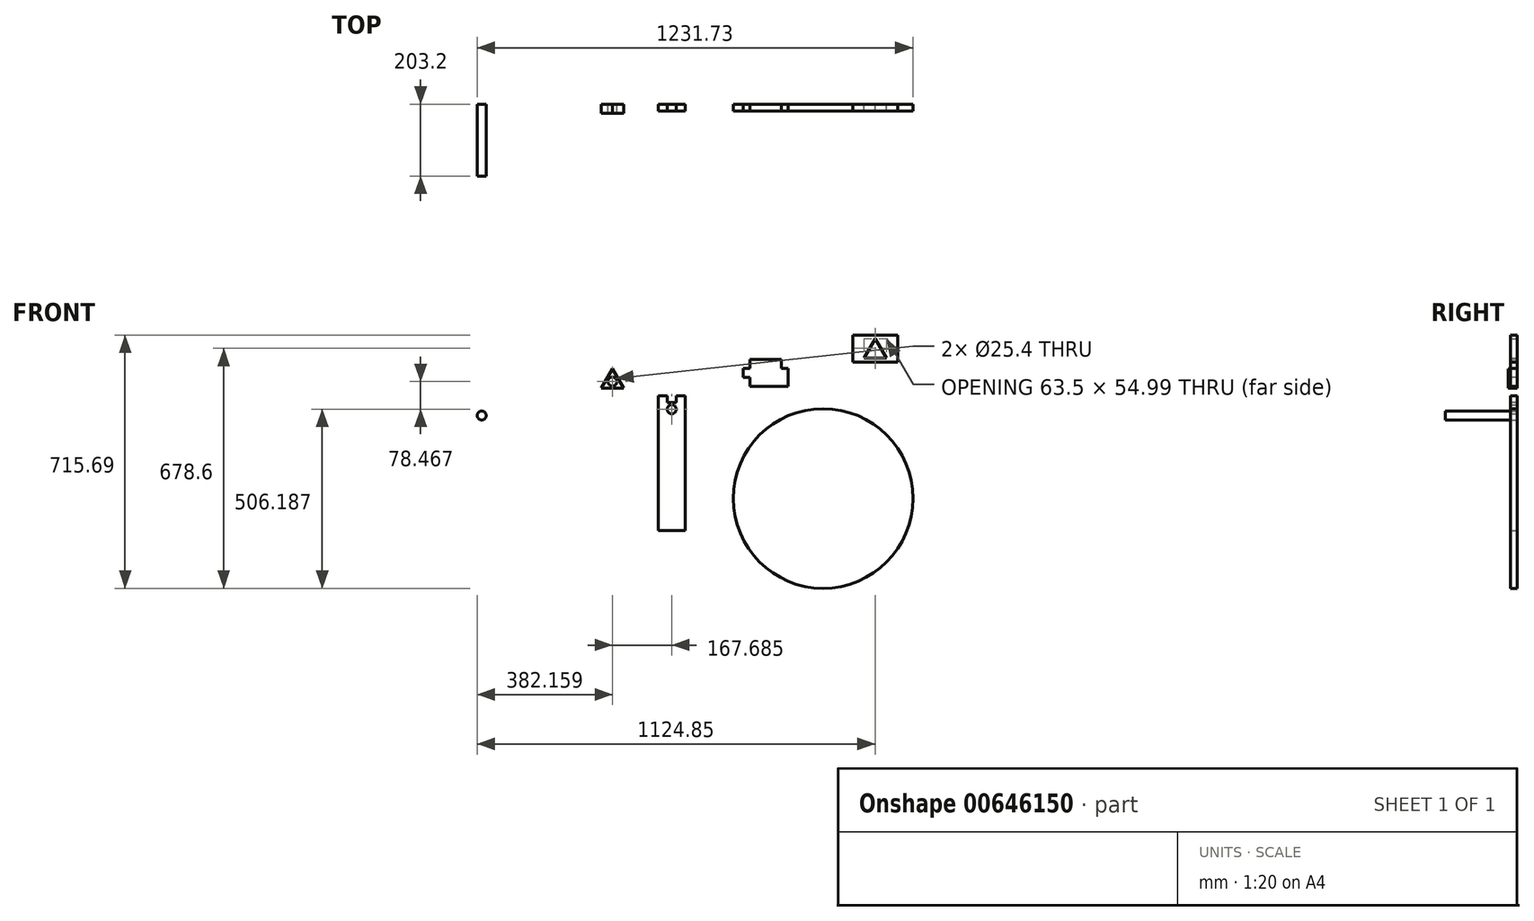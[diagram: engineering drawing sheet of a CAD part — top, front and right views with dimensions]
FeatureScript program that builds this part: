
annotation { "Feature Type Name" : "Feature", "Feature Type Description" : "" }
export const myFeature = defineFeature(function(context is Context, id is Id, definition is map)
    precondition{}
    {
        {
            var Q0;
            Q0=qCreatedBy(makeId("Front.planeOp"),FACE);
            var sketch = newSketch(context, id + "F0", { "sketchPlane" : qUnion([Q0])});
            skLineSegment(sketch, "E0.bottom", {"start": v(-82.53, 327.54) * mm, "end": v(-6.33, 327.54) * mm});
            skLineSegment(sketch, "E0.top", {"start": v(-82.53, -53.46) * mm, "end": v(-6.33, -53.46) * mm});
            skLineSegment(sketch, "E0.left", {"start": v(-82.53, 327.54) * mm, "end": v(-82.53, -53.46) * mm});
            skLineSegment(sketch, "E0.right", {"start": v(-6.33, 327.54) * mm, "end": v(-6.33, -53.46) * mm});
            skCircle(sketch, "E1", {"center": v(-44.43, 289.44) * mm, "radius": 12.7 * mm});
            skLineSegment(sketch, "E2.bottom", {"start": v(-82.53, 327.54) * mm, "end": v(-69.83, 327.54) * mm});
            skLineSegment(sketch, "E2.top", {"start": v(-82.53, 308.49) * mm, "end": v(-69.83, 308.49) * mm});
            skLineSegment(sketch, "E2.left", {"start": v(-82.53, 327.54) * mm, "end": v(-82.53, 308.49) * mm});
            skLineSegment(sketch, "E3.bottom", {"start": v(-69.83, 327.54) * mm, "end": v(-57.13, 327.54) * mm});
            skLineSegment(sketch, "E3.top", {"start": v(-69.83, 308.49) * mm, "end": v(-57.13, 308.49) * mm});
            skLineSegment(sketch, "E3.right", {"start": v(-57.13, 327.54) * mm, "end": v(-57.13, 308.49) * mm});
            skLineSegment(sketch, "E4.bottom", {"start": v(-57.13, 327.54) * mm, "end": v(-44.43, 327.54) * mm});
            skLineSegment(sketch, "E4.top", {"start": v(-57.13, 308.49) * mm, "end": v(-44.43, 308.49) * mm});
            skLineSegment(sketch, "E5.bottom", {"start": v(-44.43, 327.54) * mm, "end": v(-31.73, 327.54) * mm});
            skLineSegment(sketch, "E5.top", {"start": v(-44.43, 308.49) * mm, "end": v(-31.73, 308.49) * mm});
            skLineSegment(sketch, "E6.bottom", {"start": v(-31.73, 327.54) * mm, "end": v(-19.03, 327.54) * mm});
            skLineSegment(sketch, "E6.top", {"start": v(-31.73, 308.49) * mm, "end": v(-19.03, 308.49) * mm});
            skLineSegment(sketch, "E6.left", {"start": v(-31.73, 327.54) * mm, "end": v(-31.73, 308.49) * mm});
            skLineSegment(sketch, "E7.bottom", {"start": v(-19.03, 327.54) * mm, "end": v(-6.33, 327.54) * mm});
            skLineSegment(sketch, "E7.top", {"start": v(-19.03, 308.49) * mm, "end": v(-6.33, 308.49) * mm});
            skLineSegment(sketch, "E7.right", {"start": v(-6.33, 327.54) * mm, "end": v(-6.33, 308.49) * mm});
            skSolve(sketch);
        }
        {
            var Q0;
            Q0 = qSketchRegion(id + "F0", true);
            var Q1;
            Q1=makeQuery(id+"F0.imprint","IMPRINT",FACE,{"disambiguationData":[TD([[makeQuery(id+"F0.imprint","IMPRINT",EDGE,{"derivedFrom":sQuery(id+"F0.wireOp",EDGE,"E0.bottom")}),-1.0]])]});
            extrude(context, id + "F1", {"entities" : qUnion([Q0, Q1]), "depth" : 19.05 * mm, "offsetDistance" : 25.4 * mm});
        }
        {
            var Q0;
            Q0=qCreatedBy(makeId("Front.planeOp"),FACE);
            var sketch = newSketch(context, id + "F2", { "sketchPlane" : qUnion([Q0])});
            skLineSegment(sketch, "E8.bottom", {"start": v(157.89, 430.1) * mm, "end": v(284.89, 430.1) * mm});
            skLineSegment(sketch, "E8.top", {"start": v(157.89, 353.9) * mm, "end": v(284.89, 353.9) * mm});
            skLineSegment(sketch, "E8.left", {"start": v(157.89, 430.1) * mm, "end": v(157.89, 353.9) * mm});
            skLineSegment(sketch, "E8.right", {"start": v(284.89, 430.1) * mm, "end": v(284.89, 353.9) * mm});
            skSolve(sketch);
        }
        {
            var Q0;
            Q0 = qSketchRegion(id + "F2", true);
            extrude(context, id + "F3", {"entities" : qUnion([Q0]), "depth" : 19.05 * mm, "offsetDistance" : 25.4 * mm});
        }
        {
            var Q0;
            Q0=qCreatedBy(makeId("Front.planeOp"),FACE);
            var sketch = newSketch(context, id + "F4", { "sketchPlane" : qUnion([Q0])});
            skCircle(sketch, "E9", {"center": v(383.46, 37.25) * mm, "radius": 254 * mm});
            skSolve(sketch);
        }
        {
            var Q0;
            Q0 = qSketchRegion(id + "F4", true);
            extrude(context, id + "F5", {"entities" : qUnion([Q0]), "operationType" : NewBodyOperationType.ADD, "depth" : 19.05 * mm, "offsetDistance" : 25.4 * mm});
        }
        {
            var Q0;
            Q0=qCreatedBy(makeId("Front.planeOp"),FACE);
            var sketch = newSketch(context, id + "F6", { "sketchPlane" : qUnion([Q0])});
            skLineSegment(sketch, "E10.bottom", {"start": v(467.08, 498.94) * mm, "end": v(594.08, 498.94) * mm});
            skLineSegment(sketch, "E10.top", {"start": v(467.08, 422.74) * mm, "end": v(594.08, 422.74) * mm});
            skLineSegment(sketch, "E10.left", {"start": v(467.08, 498.94) * mm, "end": v(467.08, 422.74) * mm});
            skLineSegment(sketch, "E10.right", {"start": v(594.08, 498.94) * mm, "end": v(594.08, 422.74) * mm});
            skLineSegment(sketch, "E11", {"start": v(498.83, 434.35) * mm, "end": v(562.33, 434.35) * mm});
            skLineSegment(sketch, "E12", {"start": v(562.33, 434.35) * mm, "end": v(530.58, 489.35) * mm});
            skLineSegment(sketch, "E13", {"start": v(530.58, 489.35) * mm, "end": v(498.83, 434.35) * mm});
            skSolve(sketch);
        }
        {
            var Q0;
            Q0=makeQuery(id+"F6.imprint","IMPRINT",FACE,{"disambiguationData":[TD([[makeQuery(id+"F6.imprint","IMPRINT",EDGE,{"derivedFrom":sQuery(id+"F6.wireOp",EDGE,"E10.bottom")}),-1.0]])]});
            extrude(context, id + "F7", {"entities" : qUnion([Q0]), "depth" : 19.05 * mm, "offsetDistance" : 25.4 * mm});
        }
        {
            var Q0;
            Q0=makeQuery(id+"F1.opExtrude","CAP_FACE",FACE,{"disambiguationData":[OSD([sQuery(id+"F0.wireOp",EDGE,"E0.top"),sQuery(id+"F0.wireOp",EDGE,"E0.left"),sQuery(id+"F0.wireOp",EDGE,"E0.right"),sQuery(id+"F0.wireOp",EDGE,"E1"),sQuery(id+"F0.wireOp",EDGE,"E2.bottom"),sQuery(id+"F0.wireOp",EDGE,"E2.left"),sQuery(id+"F0.wireOp",EDGE,"E3.bottom"),sQuery(id+"F0.wireOp",EDGE,"E4.bottom"),sQuery(id+"F0.wireOp",EDGE,"E5.bottom"),sQuery(id+"F0.wireOp",EDGE,"E6.bottom"),sQuery(id+"F0.wireOp",EDGE,"E7.bottom"),sQuery(id+"F0.wireOp",EDGE,"E7.right")])],"isStart":false});
            var sketch = newSketch(context, id + "F8", { "sketchPlane" : qUnion([Q0])});
            skLineSegment(sketch, "E14.bottom", {"start": v(-82.53, 327.54) * mm, "end": v(-57.13, 327.54) * mm});
            skLineSegment(sketch, "E14.top", {"start": v(-82.53, 308.49) * mm, "end": v(-57.13, 308.49) * mm});
            skLineSegment(sketch, "E14.left", {"start": v(-82.53, 327.54) * mm, "end": v(-82.53, 308.49) * mm});
            skLineSegment(sketch, "E14.right", {"start": v(-57.13, 327.54) * mm, "end": v(-57.13, 308.49) * mm});
            skLineSegment(sketch, "E15.bottom", {"start": v(-57.13, 327.54) * mm, "end": v(-31.73, 327.54) * mm});
            skLineSegment(sketch, "E15.top", {"start": v(-57.13, 308.49) * mm, "end": v(-31.73, 308.49) * mm});
            skLineSegment(sketch, "E15.right", {"start": v(-31.73, 327.54) * mm, "end": v(-31.73, 308.49) * mm});
            skLineSegment(sketch, "E16.bottom", {"start": v(-31.73, 327.54) * mm, "end": v(-6.33, 327.54) * mm});
            skLineSegment(sketch, "E16.top", {"start": v(-31.73, 308.49) * mm, "end": v(-6.33, 308.49) * mm});
            skLineSegment(sketch, "E16.right", {"start": v(-6.33, 327.54) * mm, "end": v(-6.33, 308.49) * mm});
            skSolve(sketch);
        }
        {
            var Q0;
            Q0=makeQuery(id+"F8.imprint","IMPRINT",FACE,{"disambiguationData":[TD([[makeQuery(id+"F8.imprint","IMPRINT",EDGE,{"derivedFrom":sQuery(id+"F8.wireOp",EDGE,"E15.bottom")}),-1.0]])]});
            extrude(context, id + "F9", {"entities" : qUnion([Q0]), "operationType" : NewBodyOperationType.REMOVE, "oppositeDirection" : true, "depth" : 25.4 * mm, "offsetDistance" : 25.4 * mm});
        }
        {
            var Q0;
            Q0=makeQuery(id+"F3.opExtrude","CAP_FACE",FACE,{"disambiguationData":[OSD([sQuery(id+"F2.wireOp",EDGE,"E8.bottom"),sQuery(id+"F2.wireOp",EDGE,"E8.top"),sQuery(id+"F2.wireOp",EDGE,"E8.left"),sQuery(id+"F2.wireOp",EDGE,"E8.right")])],"isStart":false});
            var sketch = newSketch(context, id + "F10", { "sketchPlane" : qUnion([Q0])});
            skLineSegment(sketch, "E17.bottom", {"start": v(157.89, 430.1) * mm, "end": v(176.94, 430.1) * mm});
            skLineSegment(sketch, "E17.top", {"start": v(157.89, 404.7) * mm, "end": v(176.94, 404.7) * mm});
            skLineSegment(sketch, "E17.left", {"start": v(157.89, 430.1) * mm, "end": v(157.89, 404.7) * mm});
            skLineSegment(sketch, "E17.right", {"start": v(176.94, 430.1) * mm, "end": v(176.94, 404.7) * mm});
            skLineSegment(sketch, "E18.top", {"start": v(157.89, 379.3) * mm, "end": v(176.94, 379.3) * mm});
            skLineSegment(sketch, "E18.left", {"start": v(157.89, 404.7) * mm, "end": v(157.89, 379.3) * mm});
            skLineSegment(sketch, "E18.right", {"start": v(176.94, 404.7) * mm, "end": v(176.94, 379.3) * mm});
            skLineSegment(sketch, "E19.top", {"start": v(157.89, 353.9) * mm, "end": v(176.94, 353.9) * mm});
            skLineSegment(sketch, "E19.left", {"start": v(157.89, 379.3) * mm, "end": v(157.89, 353.9) * mm});
            skLineSegment(sketch, "E19.right", {"start": v(176.94, 379.3) * mm, "end": v(176.94, 353.9) * mm});
            skLineSegment(sketch, "E20.bottom", {"start": v(284.89, 430.1) * mm, "end": v(265.84, 430.1) * mm});
            skLineSegment(sketch, "E20.top", {"start": v(284.89, 404.7) * mm, "end": v(265.84, 404.7) * mm});
            skLineSegment(sketch, "E20.left", {"start": v(284.89, 430.1) * mm, "end": v(284.89, 404.7) * mm});
            skLineSegment(sketch, "E20.right", {"start": v(265.84, 430.1) * mm, "end": v(265.84, 404.7) * mm});
            skLineSegment(sketch, "E21.bottom", {"start": v(265.84, 404.7) * mm, "end": v(284.89, 404.7) * mm});
            skLineSegment(sketch, "E21.top", {"start": v(265.84, 379.3) * mm, "end": v(284.89, 379.3) * mm});
            skLineSegment(sketch, "E21.left", {"start": v(265.84, 404.7) * mm, "end": v(265.84, 379.3) * mm});
            skLineSegment(sketch, "E21.right", {"start": v(284.89, 404.7) * mm, "end": v(284.89, 379.3) * mm});
            skLineSegment(sketch, "E22.top", {"start": v(265.84, 353.9) * mm, "end": v(284.89, 353.9) * mm});
            skLineSegment(sketch, "E22.left", {"start": v(265.84, 379.3) * mm, "end": v(265.84, 353.9) * mm});
            skLineSegment(sketch, "E22.right", {"start": v(284.89, 379.3) * mm, "end": v(284.89, 353.9) * mm});
            skSolve(sketch);
        }
        {
            var Q0;
            Q0=makeQuery(id+"F10.imprint","IMPRINT",FACE,{"disambiguationData":[TD([[makeQuery(id+"F10.imprint","IMPRINT",EDGE,{"derivedFrom":sQuery(id+"F10.wireOp",EDGE,"E17.bottom")}),-1.0]])]});
            var Q1;
            Q1=makeQuery(id+"F10.imprint","IMPRINT",FACE,{"disambiguationData":[TD([[makeQuery(id+"F10.imprint","IMPRINT",EDGE,{"derivedFrom":sQuery(id+"F10.wireOp",EDGE,"E18.top")}),-1.0]])]});
            var Q2;
            Q2=makeQuery(id+"F10.imprint","IMPRINT",FACE,{"disambiguationData":[TD([[makeQuery(id+"F10.imprint","IMPRINT",EDGE,{"derivedFrom":sQuery(id+"F10.wireOp",EDGE,"E21.top")}),-1.0]])]});
            var Q3;
            Q3=makeQuery(id+"F10.imprint","IMPRINT",FACE,{"disambiguationData":[TD([[makeQuery(id+"F10.imprint","IMPRINT",EDGE,{"derivedFrom":sQuery(id+"F10.wireOp",EDGE,"E20.bottom")}),-1.0]])]});
            extrude(context, id + "F11", {"entities" : qUnion([Q0, Q1, Q2, Q3]), "operationType" : NewBodyOperationType.REMOVE, "oppositeDirection" : true, "depth" : 25.4 * mm, "offsetDistance" : 25.4 * mm});
        }
        {
            var Q0;
            Q0=qCreatedBy(makeId("Front.planeOp"),FACE);
            var sketch = newSketch(context, id + "F12", { "sketchPlane" : qUnion([Q0])});
            skLineSegment(sketch, "E23", {"start": v(-244, 348.85) * mm, "end": v(-180.5, 348.85) * mm});
            skLineSegment(sketch, "E24", {"start": v(-180.5, 348.85) * mm, "end": v(-212.25, 403.85) * mm});
            skLineSegment(sketch, "E25", {"start": v(-212.25, 403.85) * mm, "end": v(-244, 348.85) * mm});
            skCircle(sketch, "E26", {"center": v(-212.11, 367.9) * mm, "radius": 12.7 * mm});
            skSolve(sketch);
        }
        {
            var Q0;
            Q0=makeQuery(id+"F12.imprint","IMPRINT",FACE,{"disambiguationData":[TD([[makeQuery(id+"F12.imprint","IMPRINT",EDGE,{"derivedFrom":sQuery(id+"F12.wireOp",EDGE,"E23")}),1.0]])]});
            extrude(context, id + "F13", {"entities" : qUnion([Q0]), "depth" : 25.4 * mm, "offsetDistance" : 25.4 * mm});
        }
        {
            var Q0;
            Q0=qCreatedBy(makeId("Front.planeOp"),FACE);
            var sketch = newSketch(context, id + "F14", { "sketchPlane" : qUnion([Q0])});
            skCircle(sketch, "E27", {"center": v(-581.57, 271.85) * mm, "radius": 12.7 * mm});
            skSolve(sketch);
        }
        {
            var Q0;
            Q0=makeQuery(id+"F14.imprint","IMPRINT",FACE,{"disambiguationData":[TD([[makeQuery(id+"F14.imprint","IMPRINT",EDGE,{"derivedFrom":sQuery(id+"F14.wireOp",EDGE,"E27")}),1.0]])]});
            extrude(context, id + "F15", {"entities" : qUnion([Q0]), "depth" : 203.2 * mm, "offsetDistance" : 25.4 * mm});
        }
    });
